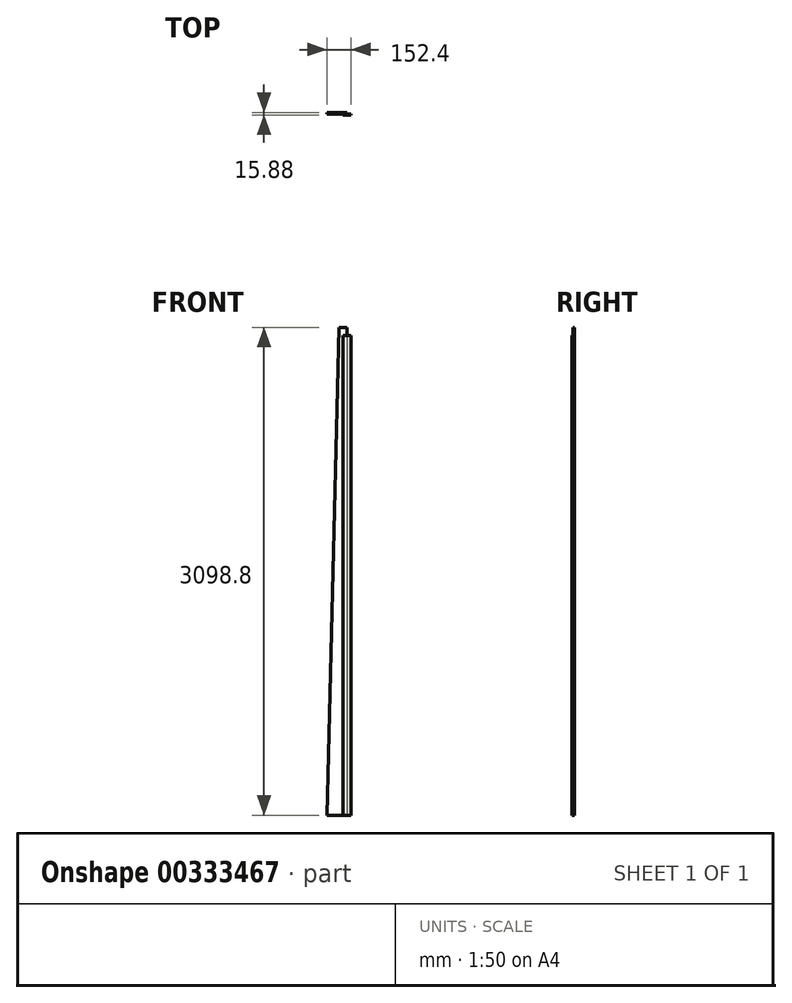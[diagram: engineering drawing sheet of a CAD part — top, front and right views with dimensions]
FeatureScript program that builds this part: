
annotation { "Feature Type Name" : "Feature", "Feature Type Description" : "" }
export const myFeature = defineFeature(function(context is Context, id is Id, definition is map)
    precondition{}
    {
        {
            var Q0;
            Q0=qCreatedBy(makeId("Front.planeOp"),FACE);
            var sketch = newSketch(context, id + "F0", { "sketchPlane" : qUnion([Q0])});
            skLineSegment(sketch, "E0.bottom", {"start": v(-50.8, 3048) * mm, "end": v(0, 3048) * mm});
            skLineSegment(sketch, "E0.top", {"start": v(-50.8, 0) * mm, "end": v(0, 0) * mm});
            skLineSegment(sketch, "E0.left", {"start": v(-50.8, 3048) * mm, "end": v(-50.8, 0) * mm});
            skLineSegment(sketch, "E0.right", {"start": v(0, 3048) * mm, "end": v(0, 0) * mm});
            skSolve(sketch);
        }
        {
            var Q0;
            Q0 = qSketchRegion(id + "F0", true);
            extrude(context, id + "F1", {"entities" : qUnion([Q0]), "depth" : 6.35 * mm});
        }
        {
            var Q0;
            Q0=makeQuery(id+"F1.opExtrude","CAP_FACE",FACE,{"disambiguationData":[OSD([sQuery(id+"F0.wireOp",EDGE,"E0.bottom"),sQuery(id+"F0.wireOp",EDGE,"E0.top"),sQuery(id+"F0.wireOp",EDGE,"E0.left"),sQuery(id+"F0.wireOp",EDGE,"E0.right")])],"isStart":true});
            var sketch = newSketch(context, id + "F2", { "sketchPlane" : qUnion([Q0])});
            skLineSegment(sketch, "E1", {"start": v(76.2, 3098.8) * mm, "end": v(25.4, 3098.8) * mm});
            skLineSegment(sketch, "E2", {"start": v(25.4, 3098.8) * mm, "end": v(25.4, 0) * mm});
            skLineSegment(sketch, "E3", {"start": v(25.4, 0) * mm, "end": v(152.4, 0) * mm});
            skLineSegment(sketch, "E4", {"start": v(152.4, 0) * mm, "end": v(76.2, 3098.8) * mm});
            skSolve(sketch);
        }
        {
            var Q0;
            Q0 = qSketchRegion(id + "F2", true);
            extrude(context, id + "F3", {"entities" : qUnion([Q0]), "operationType" : NewBodyOperationType.ADD, "depth" : 9.52 * mm});
        }
    });
